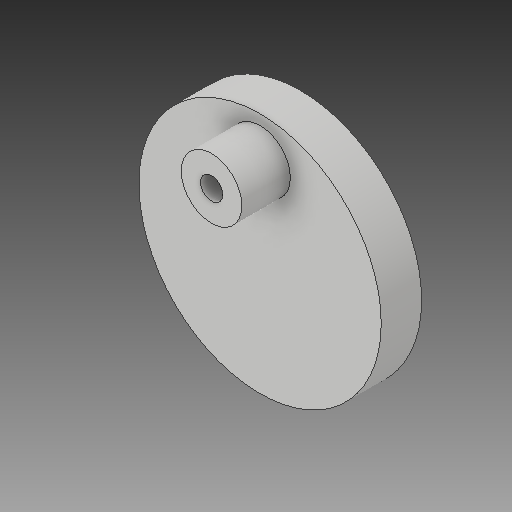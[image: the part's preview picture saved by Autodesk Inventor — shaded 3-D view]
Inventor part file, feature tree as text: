
AUTODESK INVENTOR PART (.ipt)
format: ipt  version: 2019 (Build 230136000, 136)  size: 110,080 bytes
history: native  units: in
note: dims shown in document units (in); Inventor stores cm internally (conversion verified against a paired STEP export)
features: extrude x2, sketch x2
ambient origin geometry x8: Origin, YZ Plane, XZ Plane, XY Plane, X Axis, Y Axis, Z Axis, Center Point
bodies: Solid1 (feature_tree)
feature tree (4):
  extrude  "Extrusion1"  Depth=0.3937in TaperAngle=0.0deg
  extrude  "Extrusion2"  Depth=0.4724in
  sketch  "Sketch1"  dims[d0=2.3622in d1=0.3937in d2=0.0in]
  sketch  "Sketch2"  dims[d3=0.5906in d4=0.2165in d5=0.4724in d6=0.0in]
